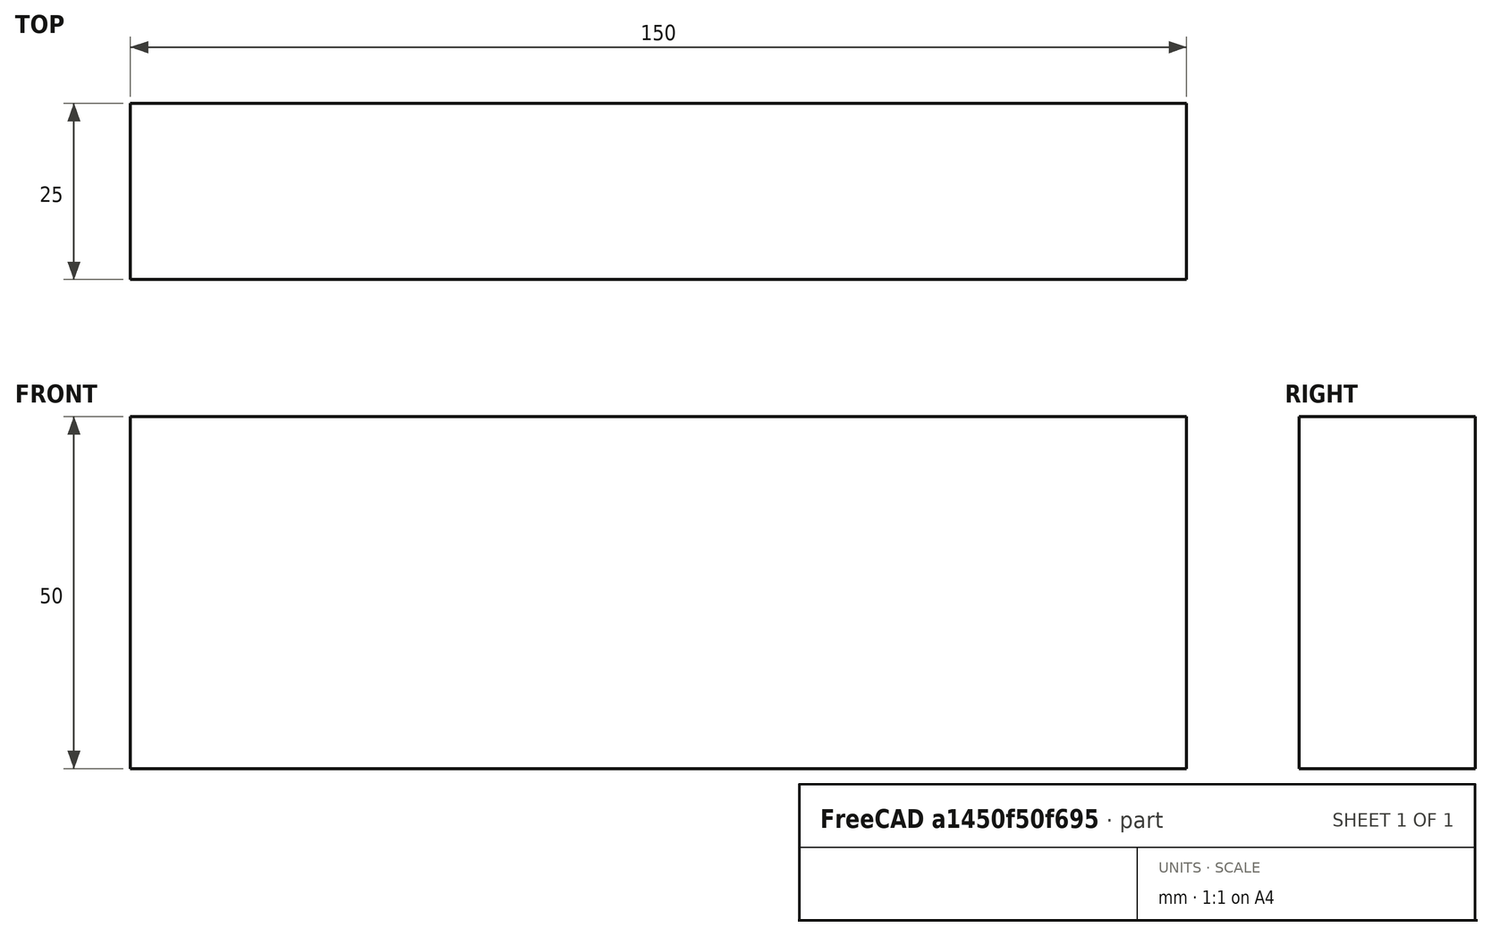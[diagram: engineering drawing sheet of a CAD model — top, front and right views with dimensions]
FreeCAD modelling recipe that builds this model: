
FCSTD DOCUMENT  (FreeCAD 0.15R4671 (Git))
Label: Flat Bar 150x25 EN10058 S235JR
License: All rights reserved
LicenseURL: http://en.wikipedia.org/wiki/All_rights_reserved
objects: Sketcher::SketchObject×1, Part::Extrusion×1
note: 2 computed .brp shape members not serialized (recipe doc carries the construction recipe); baked Part::Feature solids carry a one-line shape summary decoded from their .brp

FEATURE [Sketcher::SketchObject] Sketch
  sketch-geometry (4):
    g0: LineSegment StartX=-75 StartY=-12.5 StartZ=0 EndX=75 EndY=-12.5 EndZ=0
    g1: LineSegment StartX=75 StartY=-12.5 StartZ=0 EndX=75 EndY=12.5 EndZ=0
    g2: LineSegment StartX=75 StartY=12.5 StartZ=0 EndX=-75 EndY=12.5 EndZ=0
    g3: LineSegment StartX=-75 StartY=12.5 StartZ=0 EndX=-75 EndY=-12.5 EndZ=0
  constraints (12):
    c: Coincident(g0,g1)
    c: Coincident(g1,g2)
    c: Coincident(g2,g3)
    c: Coincident(g3,g0)
    c: Horizontal(g0)
    c: Horizontal(g2)
    c: Vertical(g1)
    c: Vertical(g3)
    c: Symmetric(g1,g2,g-2)
    c: Symmetric(g0,g1,g-1)
    c: DistanceY(g1) = 25
    c: DistanceX(g0) = 150
FEATURE [Part::Extrusion] Extrude  label="Flat Bar 150x25 EN10058 S235JR"
  Base = -> Sketch
  Dir = (0,0,50)
  Solid = true
